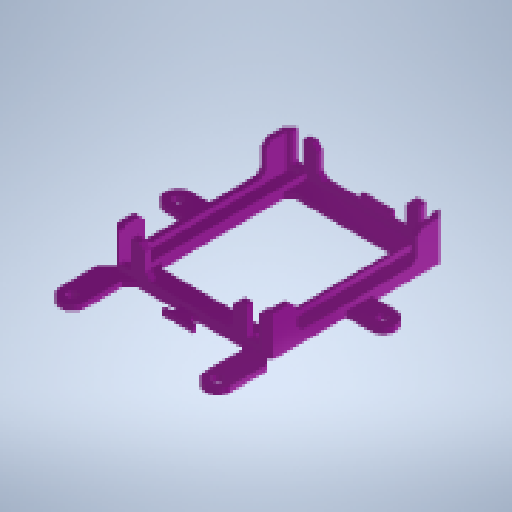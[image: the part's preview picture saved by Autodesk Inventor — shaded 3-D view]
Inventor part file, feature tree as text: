
AUTODESK INVENTOR PART (.ipt)
format: ipt  version: 2025.3 (Build 293356030, 356C)  size: 525,824 bytes
history: native  units: mm
features: extrude x6, chamfer x6, sketch x3, other x1
ambient origin geometry x8: Origin, YZ Plane, XZ Plane, XY Plane, X Axis, Y Axis, Z Axis, Center Point
bodies: Body1 (feature_tree)
feature tree (16):
  other  "ソリッド1"
  sketch  "スケッチ1"
  extrude  "ベース"  Depth=10.0mm
  extrude  "壁"  Depth=35.0mm
  extrude  "壁切り欠き"  Depth=51.0mm
  extrude  "輪ゴムフック"  Depth=23.0mm
  extrude  "補強"  Depth=43.0mm
  chamfer  "面取り1"  Distance=72.0mm
  chamfer  "面取り2"  Distance=9.0mm
  chamfer  "面取り3"  Distance=2.0mm
  chamfer  "面取り4"  Distance=2.0mm
  extrude  "コード取り出し"  TaperAngle=135.0deg  [1 undecoded]
  chamfer  "面取り5"  Angle=135.0deg  [1 undecoded]
  chamfer  "面取り6"  Distance=6.0mm
  sketch  "スケッチ4"
  sketch  "スケッチ5"
note: 2 required parameter values undecoded (feature->parameter linkage not recoverable at this tier; creation-order binding heuristic only, values carry confidence <= 0.55)
